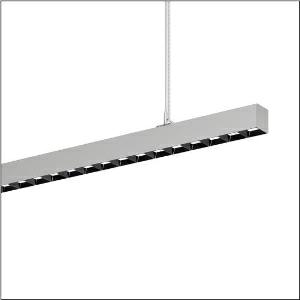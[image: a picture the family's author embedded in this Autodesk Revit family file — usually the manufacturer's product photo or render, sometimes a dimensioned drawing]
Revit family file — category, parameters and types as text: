
# Revit family: silica_r__21_51mx31tat7s_2b6e
name_source: partatom
category: Lighting Fixtures
units: mm (PartAtom-declared; Revit-internal decimal feet)

## family parameters
Cut with Voids When Loaded = No
Host = Face
Light Source = No
Part Type = Normal
Room Calculation Point = No
Round Connector Dimension = Use Diameter
Shared = No

## types (1)
- --- (1 x LED, 6220 lm, 53.5 W, 6500K)
    Apparent Load = 54 VA
    CIE Flux Codes = 85 99 100 60 100
    Color Rendering = 80
    Color Temperature = 6500K
    Default Elevation = 1800 mm
    Description = Silica® 21, office luminaire, primary light control with darklight reflector, of PMMA, black, CAT 2 (L<= 3000cd/m²), light emission: direct/indirect distribution, primary light characteristic: symmetric, installation type: suspended mounting, LED, rated luminous flux: 6.220lm, luminous efficacy: 111lm/W, light colour: 8tw, colour temperature: 2700..6500K, control gear: ECG DALI, with terminal, 3+2-pole, max. 2.5mm², mains connection: 220..240V, AC, 50/60Hz, rated input power: 56.2W, luminaire housing, of aluminium, metallic grey (RAL 9006), length: 1.204mm, width: 53mm, height: 53mm, protection rating (complete): IP20, insulation class (complete): insulation class I (protective earthing), certification: CE, permissible operating ambient temperature: 0..+35°C, standard: EN 50419, packaging unit: 1 piece
    Height = 53 mm
    Lamp = 1 x LED
    Lamp Light Flux = 6220 lm
    Lamp Power = 53.5 W
    Lamp count = 1
    Length = 1204 mm
    Luminous efficacy = 116 lm/W
    Manufacturer = Siteco
    ModVariant = No
    Model = 51MX31TAT7S
    Mounting Place = Ceiling
    Mounting Type = Pendant
    Number of Poles = 1
    OnlyDefault = Yes
    Power Factor = 1
    Product Name = Silica® 21
    Product group = office luminaire | ceiling pendant
    ProductGroupID = 902
    Protection Class = Protection class I
    Protection Degree = IP 20
    RLX_Detail_Level = 1
    RLX_Emergency_Light_Flux = 0 lm
    RLX_Emergency_Type = 0
    RLX_Emergency_Type_DB = No
    RlxData = <blob elided: 41321 chars, md5=67ddc3b2>
    Socket = socket
    Standby Power = 0 W
    System Light Flux = 6220 lm
    System Power = 54 W
    Type Comments = individual setting
    Type Image = l_1313642.jpg
    URL = http://relux.com
    VarID = @adj_089241
    Voltage = 0 V
    Weight = 0.00 kg
    Width = 53 mm

## geometry (parser evidence)
native form markers: Blend x4, Sweep x11
no freeform markers — native parametric forms only
